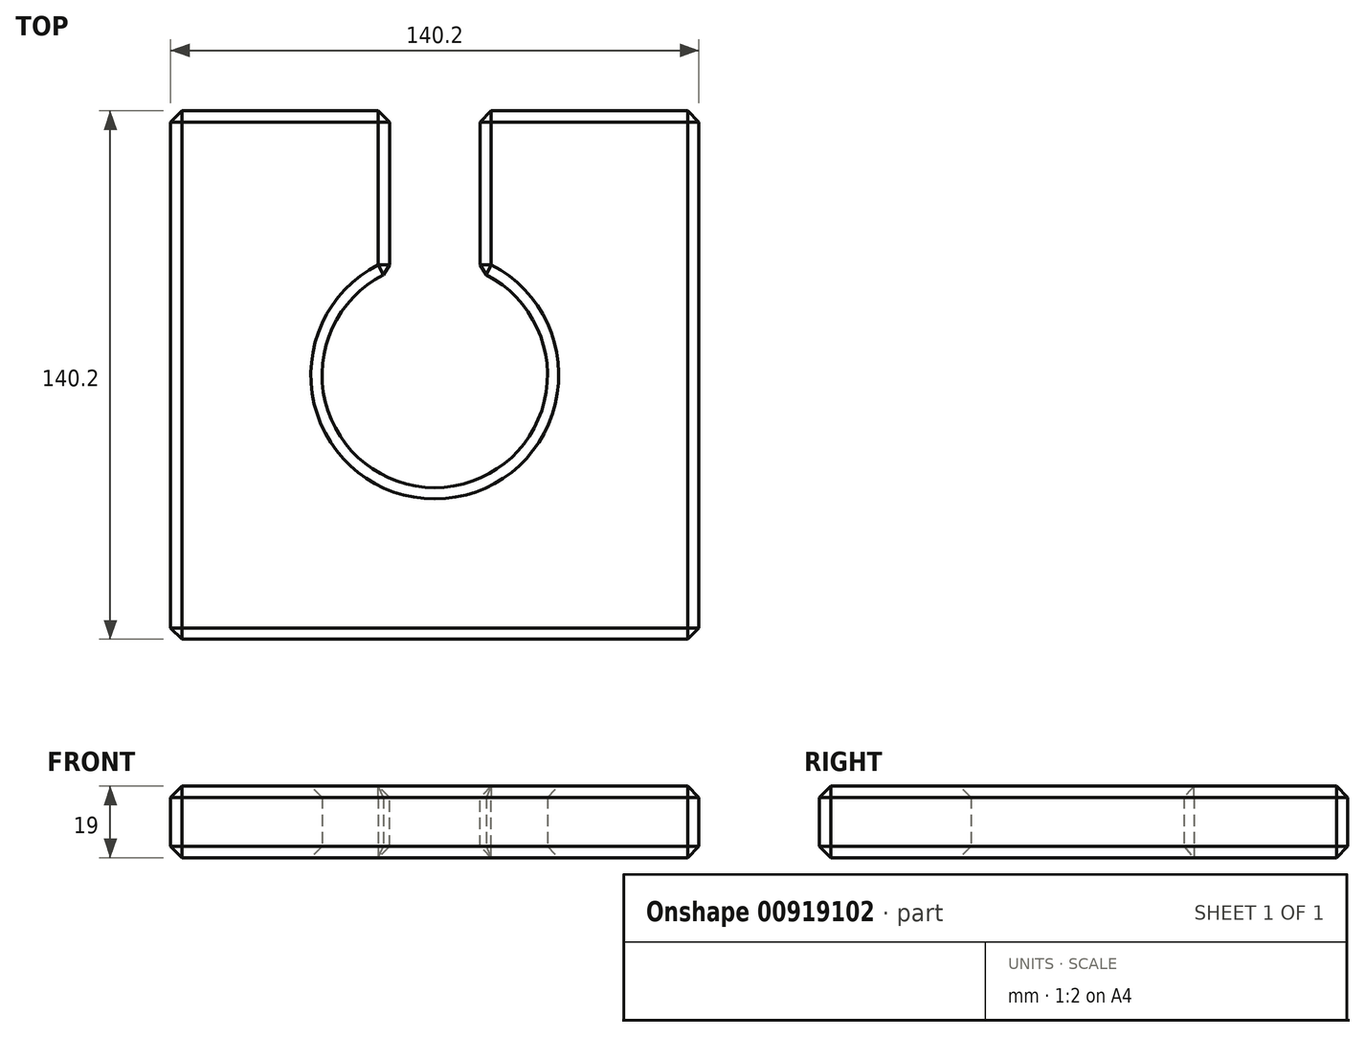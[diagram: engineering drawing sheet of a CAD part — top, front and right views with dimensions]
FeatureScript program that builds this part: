
annotation { "Feature Type Name" : "Feature", "Feature Type Description" : "" }
export const myFeature = defineFeature(function(context is Context, id is Id, definition is map)
    precondition{}
    {
        {
            var Q0;
            Q0=qCreatedBy(makeId("Top.planeOp"),FACE);
            var sketch = newSketch(context, id + "F0", { "sketchPlane" : qUnion([Q0])});
            skLineSegment(sketch, "E0.bottom", {"start": v(70.1, -70.1) * mm, "end": v(-70.1, -70.1) * mm});
            skLineSegment(sketch, "E0.top", {"start": v(70.1, 70.1) * mm, "end": v(-70.1, 70.1) * mm});
            skLineSegment(sketch, "E0.left", {"start": v(70.1, -70.1) * mm, "end": v(70.1, 70.1) * mm});
            skLineSegment(sketch, "E0.right", {"start": v(-70.1, -70.1) * mm, "end": v(-70.1, 70.1) * mm});
            skPoint(sketch, "E0.middle", {"position": v(0, 0) * mm});
            skCircle(sketch, "E1", {"center": v(0, 0) * mm, "radius": 29.9 * mm});
            skSolve(sketch);
        }
        {
            var Q0;
            Q0=makeQuery(id+"F0.imprint","IMPRINT",FACE,{"disambiguationData":[TD([[makeQuery(id+"F0.imprint","IMPRINT",EDGE,{"derivedFrom":sQuery(id+"F0.wireOp",EDGE,"E0.bottom")}),-1.0]])]});
            extrude(context, id + "F1", {"entities" : qUnion([Q0]), "depth" : 19 * mm, "offsetDistance" : 25 * mm});
        }
        {
            var Q0;
            Q0=makeQuery(id+"F1.opExtrude","CAP_FACE",FACE,{"disambiguationData":[OSD([sQuery(id+"F0.wireOp",EDGE,"E0.bottom"),sQuery(id+"F0.wireOp",EDGE,"E0.top"),sQuery(id+"F0.wireOp",EDGE,"E0.left"),sQuery(id+"F0.wireOp",EDGE,"E0.right"),sQuery(id+"F0.wireOp",EDGE,"E1")])],"isStart":false});
            var sketch = newSketch(context, id + "F2", { "sketchPlane" : qUnion([Q0])});
            skLineSegment(sketch, "E2.bottom", {"start": v(-12, 70.1) * mm, "end": v(12, 70.1) * mm});
            skLineSegment(sketch, "E2.top", {"start": v(-12, -70.1) * mm, "end": v(12, -70.1) * mm});
            skLineSegment(sketch, "E2.left", {"start": v(-12, 70.1) * mm, "end": v(-12, -70.1) * mm});
            skLineSegment(sketch, "E2.right", {"start": v(12, 70.1) * mm, "end": v(12, -70.1) * mm});
            skLineSegment(sketch, "E3", {"start": v(0, 70.1) * mm, "end": v(0, -70.1) * mm, "construction": true});
            skSolve(sketch);
        }
        {
            var Q0;
            {var subQ0=sQuery(id+"F2.wireOp",EDGE,"E2.bottom");Q0=makeQuery(id+"F2.imprint","IMPRINT",FACE,{"disambiguationData":[TD([[makeQuery(id+"F2.imprint","IMPRINT",EDGE,{"derivedFrom":subQ0}),1.0]])]});}
            extrude(context, id + "F3", {"entities" : qUnion([Q0]), "operationType" : NewBodyOperationType.REMOVE, "oppositeDirection" : true, "depth" : 19 * mm, "offsetDistance" : 25 * mm});
        }
        {
            var Q0;
            Q0=makeQuery(id+"F3.boolean.opBoolean","COPY",FACE,{"derivedFrom":makeQuery(id+"F3.opExtrude","SWEPT_FACE",FACE,{"disambiguationData":[OSD([sQuery(id+"F2.wireOp",EDGE,"E2.right")])]})});
            var Q1;
            {var subQ2=sQuery(id+"F0.wireOp",EDGE,"E0.left");var subQ3=sQuery(id+"F0.wireOp",EDGE,"E0.top");Q1=makeQuery(id+"F3.boolean.opBoolean","SPLIT",FACE,{"disambiguationData":[TD([makeQuery(id+"F1.opExtrude","SWEPT_FACE",FACE,{"disambiguationData":[OSD([subQ2])]})])],"derivedFrom":makeQuery(id+"F1.opExtrude","SWEPT_FACE",FACE,{"disambiguationData":[OSD([subQ3])]})});}
            var Q2;
            Q2=makeQuery(id+"F1.opExtrude","CAP_FACE",FACE,{"disambiguationData":[OSD([sQuery(id+"F0.wireOp",EDGE,"E0.bottom"),sQuery(id+"F0.wireOp",EDGE,"E0.top"),sQuery(id+"F0.wireOp",EDGE,"E0.left"),sQuery(id+"F0.wireOp",EDGE,"E0.right"),sQuery(id+"F0.wireOp",EDGE,"E1")])],"isStart":false});
            var Q3;
            Q3=makeQuery(id+"F1.opExtrude","CAP_FACE",FACE,{"disambiguationData":[OSD([sQuery(id+"F0.wireOp",EDGE,"E0.bottom"),sQuery(id+"F0.wireOp",EDGE,"E0.top"),sQuery(id+"F0.wireOp",EDGE,"E0.left"),sQuery(id+"F0.wireOp",EDGE,"E0.right"),sQuery(id+"F0.wireOp",EDGE,"E1")])],"isStart":true});
            var Q4;
            Q4=makeQuery(id+"F1.opExtrude","CAP_EDGE",EDGE,{"disambiguationData":[OSD([sQuery(id+"F0.wireOp",EDGE,"E1")])],"isStart":true});
            var Q5;
            Q5=makeQuery(id+"F1.opExtrude","SWEPT_FACE",FACE,{"disambiguationData":[OSD([sQuery(id+"F0.wireOp",EDGE,"E0.right")])]});
            var Q6;
            Q6=makeQuery(id+"F3.boolean.opBoolean","COPY",FACE,{"derivedFrom":makeQuery(id+"F3.opExtrude","SWEPT_FACE",FACE,{"disambiguationData":[OSD([sQuery(id+"F2.wireOp",EDGE,"E2.left")])]})});
            var Q7;
            Q7=makeQuery(id+"F1.opExtrude","SWEPT_FACE",FACE,{"disambiguationData":[OSD([sQuery(id+"F0.wireOp",EDGE,"E1")])]});
            var Q8;
            Q8=makeQuery(id+"F1.opExtrude","CAP_EDGE",EDGE,{"disambiguationData":[OSD([sQuery(id+"F0.wireOp",EDGE,"E1")])],"isStart":false});
            var Q9;
            Q9=makeQuery(id+"F1.opExtrude","SWEPT_FACE",FACE,{"disambiguationData":[OSD([sQuery(id+"F0.wireOp",EDGE,"E0.left")])]});
            var Q10;
            Q10=makeQuery(id+"F1.opExtrude","SWEPT_FACE",FACE,{"disambiguationData":[OSD([sQuery(id+"F0.wireOp",EDGE,"E0.bottom")])]});
            var Q11;
            Q11=makeQuery(id+"F3.boolean.opBoolean","COPY",EDGE,{"derivedFrom":makeQuery(id+"F3.opExtrude","SWEPT_EDGE",EDGE,{"disambiguationData":[OSD([sQuery(id+"F0.wireOp",EDGE,"E1"),sQuery(id+"F2.wireOp",EDGE,"E2.left")])]})});
            var Q12;
            Q12=makeQuery(id+"F1.opExtrude","CAP_EDGE",EDGE,{"disambiguationData":[OSD([sQuery(id+"F0.wireOp",EDGE,"E0.left")])],"isStart":false});
            var Q13;
            Q13=makeQuery(id+"F1.opExtrude","CAP_EDGE",EDGE,{"disambiguationData":[OSD([sQuery(id+"F0.wireOp",EDGE,"E0.right")])],"isStart":true});
            var Q14;
            {var subQ1=sQuery(id+"F0.wireOp",EDGE,"E0.right");var subQ3=sQuery(id+"F0.wireOp",EDGE,"E0.top");Q14=makeQuery(id+"F3.boolean.opBoolean","SPLIT",FACE,{"disambiguationData":[TD([makeQuery(id+"F1.opExtrude","SWEPT_FACE",FACE,{"disambiguationData":[OSD([subQ1])]})])],"derivedFrom":makeQuery(id+"F1.opExtrude","SWEPT_FACE",FACE,{"disambiguationData":[OSD([subQ3])]})});}
            var Q15;
            {var subQ0=sQuery(id+"F0.wireOp",EDGE,"E0.right");var subQ1=sQuery(id+"F0.wireOp",EDGE,"E0.top");Q15=makeQuery(id+"F3.boolean.opBoolean","SPLIT",EDGE,{"disambiguationData":[TD([makeQuery(id+"F1.opExtrude","SWEPT_FACE",FACE,{"disambiguationData":[OSD([subQ0])]})])],"derivedFrom":makeQuery(id+"F1.opExtrude","CAP_EDGE",EDGE,{"disambiguationData":[OSD([subQ1])],"isStart":false})});}
            var Q16;
            Q16=makeQuery(id+"F3.boolean.opBoolean","COPY",EDGE,{"derivedFrom":makeQuery(id+"F3.opExtrude","CAP_EDGE",EDGE,{"disambiguationData":[OSD([sQuery(id+"F2.wireOp",EDGE,"E2.left")])],"isStart":true})});
            var Q17;
            Q17=makeQuery(id+"F1.opExtrude","SWEPT_EDGE",EDGE,{"disambiguationData":[OSD([sQuery(id+"F0.wireOp",EDGE,"E0.bottom"),sQuery(id+"F0.wireOp",EDGE,"E0.left")])]});
            var Q18;
            Q18=makeQuery(id+"F1.opExtrude","CAP_EDGE",EDGE,{"disambiguationData":[OSD([sQuery(id+"F0.wireOp",EDGE,"E0.right")])],"isStart":false});
            var Q19;
            Q19=makeQuery(id+"F1.opExtrude","CAP_EDGE",EDGE,{"disambiguationData":[OSD([sQuery(id+"F0.wireOp",EDGE,"E0.bottom")])],"isStart":true});
            var Q20;
            Q20=makeQuery(id+"F1.opExtrude","SWEPT_EDGE",EDGE,{"disambiguationData":[OSD([sQuery(id+"F0.wireOp",EDGE,"E0.top"),sQuery(id+"F0.wireOp",EDGE,"E0.left")])]});
            var Q21;
            Q21=makeQuery(id+"F1.opExtrude","CAP_EDGE",EDGE,{"disambiguationData":[OSD([sQuery(id+"F0.wireOp",EDGE,"E0.bottom")])],"isStart":false});
            var Q22;
            Q22=makeQuery(id+"F1.opExtrude","CAP_EDGE",EDGE,{"disambiguationData":[OSD([sQuery(id+"F0.wireOp",EDGE,"E0.left")])],"isStart":true});
            var Q23;
            Q23=makeQuery(id+"F3.boolean.opBoolean","COPY",EDGE,{"derivedFrom":makeQuery(id+"F3.opExtrude","CAP_EDGE",EDGE,{"disambiguationData":[OSD([sQuery(id+"F2.wireOp",EDGE,"E2.right")])],"isStart":false})});
            var Q24;
            Q24=makeQuery(id+"F3.boolean.opBoolean","COPY",EDGE,{"derivedFrom":makeQuery(id+"F3.opExtrude","SWEPT_EDGE",EDGE,{"disambiguationData":[OSD([sQuery(id+"F0.wireOp",EDGE,"E1"),sQuery(id+"F2.wireOp",EDGE,"E2.right")])]})});
            var Q25;
            Q25=makeQuery(id+"F1.opExtrude","SWEPT_EDGE",EDGE,{"disambiguationData":[OSD([sQuery(id+"F0.wireOp",EDGE,"E0.bottom"),sQuery(id+"F0.wireOp",EDGE,"E0.right")])]});
            var Q26;
            Q26=makeQuery(id+"F3.boolean.opBoolean","COPY",EDGE,{"derivedFrom":makeQuery(id+"F3.opExtrude","SWEPT_EDGE",EDGE,{"disambiguationData":[OSD([sQuery(id+"F0.wireOp",EDGE,"E0.top"),sQuery(id+"F2.wireOp",EDGE,"E2.bottom"),sQuery(id+"F2.wireOp",EDGE,"E2.left")])]})});
            var Q27;
            Q27=makeQuery(id+"F3.boolean.opBoolean","COPY",EDGE,{"derivedFrom":makeQuery(id+"F3.opExtrude","CAP_EDGE",EDGE,{"disambiguationData":[OSD([sQuery(id+"F2.wireOp",EDGE,"E2.right")])],"isStart":true})});
            var Q28;
            {var subQ0=sQuery(id+"F0.wireOp",EDGE,"E0.left");var subQ1=sQuery(id+"F0.wireOp",EDGE,"E0.top");Q28=makeQuery(id+"F3.boolean.opBoolean","SPLIT",EDGE,{"disambiguationData":[TD([makeQuery(id+"F1.opExtrude","SWEPT_FACE",FACE,{"disambiguationData":[OSD([subQ0])]})])],"derivedFrom":makeQuery(id+"F1.opExtrude","CAP_EDGE",EDGE,{"disambiguationData":[OSD([subQ1])],"isStart":true})});}
            var Q29;
            Q29=makeQuery(id+"F3.boolean.opBoolean","COPY",EDGE,{"derivedFrom":makeQuery(id+"F3.opExtrude","CAP_EDGE",EDGE,{"disambiguationData":[OSD([sQuery(id+"F2.wireOp",EDGE,"E2.left")])],"isStart":false})});
            var Q30;
            {var subQ0=sQuery(id+"F0.wireOp",EDGE,"E0.right");var subQ1=sQuery(id+"F0.wireOp",EDGE,"E0.top");Q30=makeQuery(id+"F3.boolean.opBoolean","SPLIT",EDGE,{"disambiguationData":[TD([makeQuery(id+"F1.opExtrude","SWEPT_FACE",FACE,{"disambiguationData":[OSD([subQ0])]})])],"derivedFrom":makeQuery(id+"F1.opExtrude","CAP_EDGE",EDGE,{"disambiguationData":[OSD([subQ1])],"isStart":true})});}
            var Q31;
            {var subQ0=sQuery(id+"F0.wireOp",EDGE,"E0.left");var subQ1=sQuery(id+"F0.wireOp",EDGE,"E0.top");Q31=makeQuery(id+"F3.boolean.opBoolean","SPLIT",EDGE,{"disambiguationData":[TD([makeQuery(id+"F1.opExtrude","SWEPT_FACE",FACE,{"disambiguationData":[OSD([subQ0])]})])],"derivedFrom":makeQuery(id+"F1.opExtrude","CAP_EDGE",EDGE,{"disambiguationData":[OSD([subQ1])],"isStart":false})});}
            var Q32;
            Q32=makeQuery(id+"F1.opExtrude","SWEPT_EDGE",EDGE,{"disambiguationData":[OSD([sQuery(id+"F0.wireOp",EDGE,"E0.top"),sQuery(id+"F0.wireOp",EDGE,"E0.right")])]});
            var Q33;
            Q33=makeQuery(id+"F3.boolean.opBoolean","COPY",EDGE,{"derivedFrom":makeQuery(id+"F3.opExtrude","SWEPT_EDGE",EDGE,{"disambiguationData":[OSD([sQuery(id+"F0.wireOp",EDGE,"E0.top"),sQuery(id+"F2.wireOp",EDGE,"E2.bottom"),sQuery(id+"F2.wireOp",EDGE,"E2.right")])]})});
            chamfer(context, id + "F4", {"entities" : qUnion([Q0, Q1, Q2, Q3, Q4, Q5, Q6, Q7, Q8, Q9, Q10, Q11, Q12, Q13, Q14, Q15, Q16, Q17, Q18, Q19, Q20, Q21, Q22, Q23, Q24, Q25, Q26, Q27, Q28, Q29, Q30, Q31, Q32, Q33]), "width" : 3 * mm});
        }
    });
